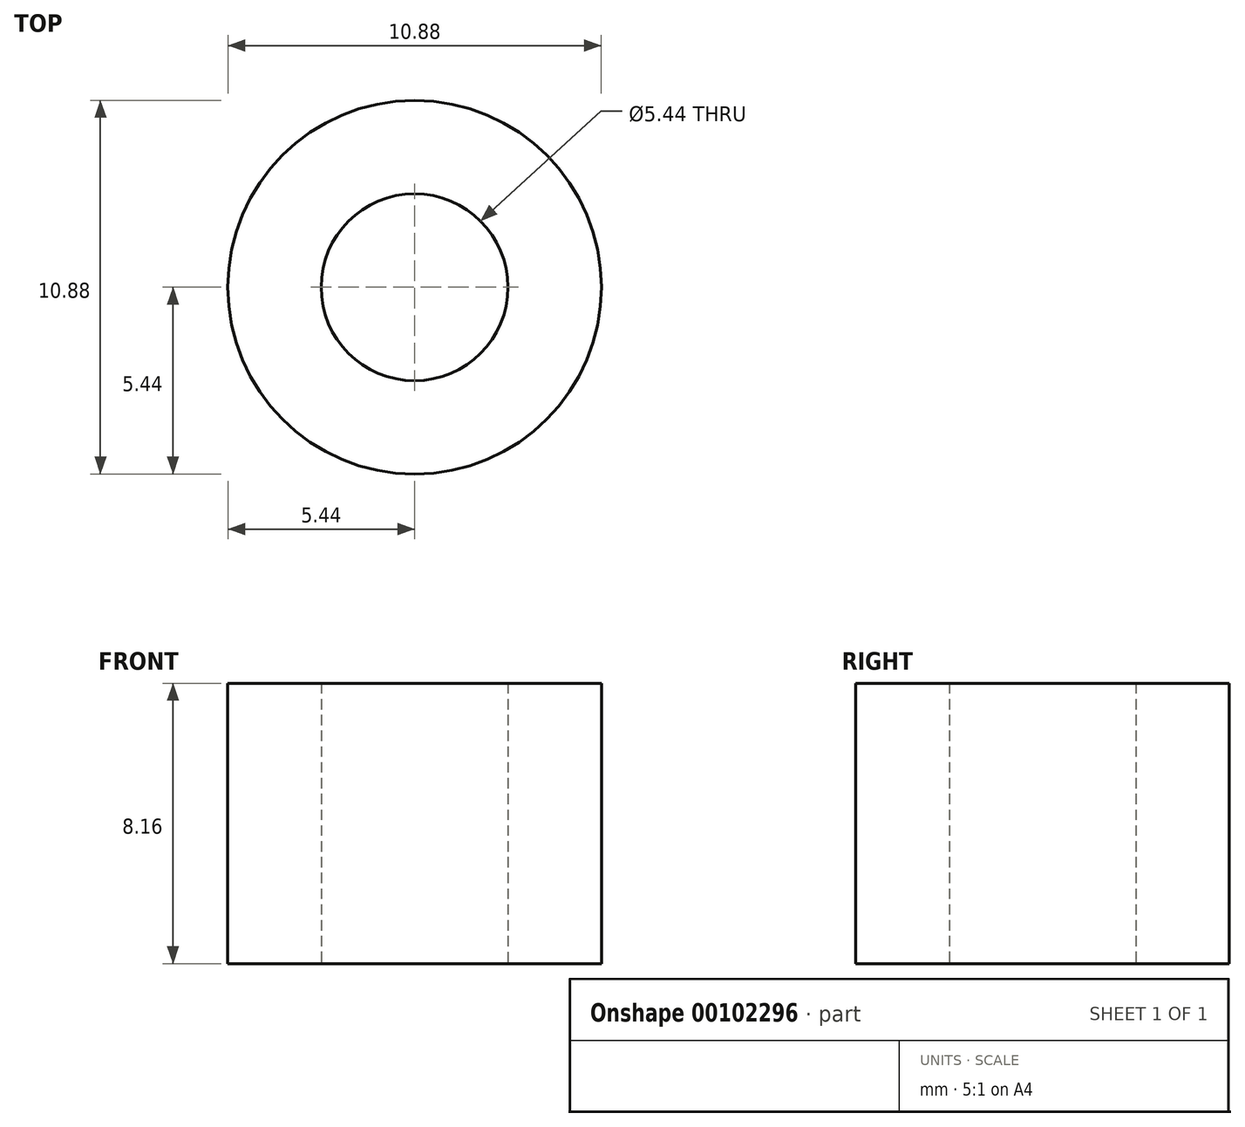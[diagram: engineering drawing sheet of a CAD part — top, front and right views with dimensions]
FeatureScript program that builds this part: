
annotation { "Feature Type Name" : "Feature", "Feature Type Description" : "" }
export const myFeature = defineFeature(function(context is Context, id is Id, definition is map)
    precondition{}
    {
        {
            var Q0;
            Q0=qCreatedBy(makeId("Top.planeOp"),FACE);
            var sketch = newSketch(context, id + "F0", { "sketchPlane" : qUnion([Q0])});
            skCircle(sketch, "E0", {"center": v(0, 0) * mm, "radius": 25.4 * mm});
            skCircle(sketch, "E1", {"center": v(0, 0) * mm, "radius": 12.7 * mm});
            skSolve(sketch);
        }
        {
            var Q0;
            Q0=qSketchRegion(id+"F0",true);
            extrude(context, id + "F1", {"entities" : qUnion([Q0]), "depth" : 38.1 * mm});
        }
        {
            var Q0;
            Q0=makeQuery(id+"F1.opExtrude","SWEPT_BODY",BODY,{"disambiguationData":[OSD([sQuery(id+"F0.wireOp",EDGE,"E0"),sQuery(id+"F0.wireOp",EDGE,"E1")])]});
            var Q1;
            Q1=qCreatedBy(makeId("Origin.pointOp"),VERTEX);
            transform(context, id + "F2", {"entities" : qUnion([Q0]), "transformType" : TransformType.SCALE_UNIFORMLY, "scale" : 6 / 28, "makeCopy" : false, "scalePoint" : qUnion([Q1])});
        }
    });
